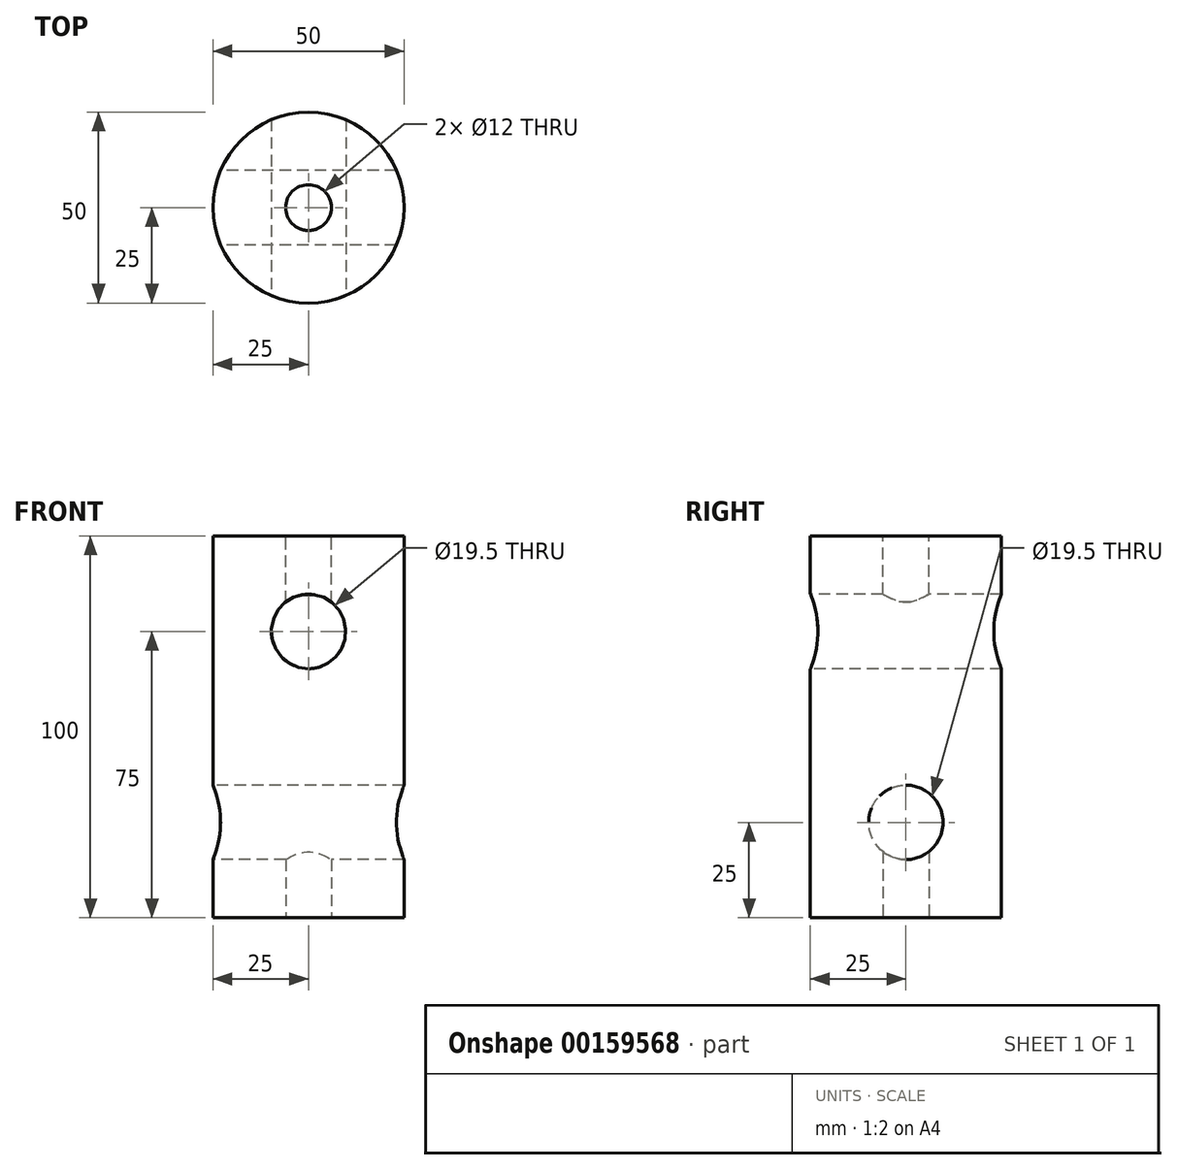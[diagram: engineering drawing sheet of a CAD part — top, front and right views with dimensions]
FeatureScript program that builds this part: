
annotation { "Feature Type Name" : "Feature", "Feature Type Description" : "" }
export const myFeature = defineFeature(function(context is Context, id is Id, definition is map)
    precondition{}
    {
        {
            var Q0;
            Q0=qCreatedBy(makeId("Top.planeOp"),FACE);
            var sketch = newSketch(context, id + "F0", { "sketchPlane" : qUnion([Q0])});
            skCircle(sketch, "E0", {"center": v(0, 0) * mm, "radius": 25 * mm});
            skSolve(sketch);
        }
        {
            var Q0;
            Q0 = qSketchRegion(id + "F0", true);
            extrude(context, id + "F1", {"entities" : qUnion([Q0]), "depth" : 100 * mm});
        }
        {
            var Q0;
            Q0=qCreatedBy(makeId("Right.planeOp"),FACE);
            var sketch = newSketch(context, id + "F2", { "sketchPlane" : qUnion([Q0])});
            skCircle(sketch, "E1", {"center": v(0, 25) * mm, "radius": 9.75 * mm});
            skSolve(sketch);
        }
        {
            var Q0;
            Q0 = qSketchRegion(id + "F2", true);
            extrude(context, id + "F3", {"entities" : qUnion([Q0]), "operationType" : NewBodyOperationType.REMOVE, "endBound" : BoundingType.THROUGH_ALL, "depth" : 25 * mm, "hasSecondDirection" : true, "secondDirectionOppositeDirection" : true, "secondDirectionDepth" : 25 * mm});
        }
        {
            var Q0;
            Q0=qCreatedBy(makeId("Front.planeOp"),FACE);
            var sketch = newSketch(context, id + "F4", { "sketchPlane" : qUnion([Q0])});
            skCircle(sketch, "E2", {"center": v(0, 75) * mm, "radius": 9.75 * mm});
            skSolve(sketch);
        }
        {
            var Q0;
            Q0 = qSketchRegion(id + "F4", true);
            extrude(context, id + "F5", {"entities" : qUnion([Q0]), "operationType" : NewBodyOperationType.REMOVE, "endBound" : BoundingType.THROUGH_ALL, "oppositeDirection" : true, "depth" : 25 * mm, "hasSecondDirection" : true, "secondDirectionOppositeDirection" : false, "secondDirectionDepth" : 25 * mm});
        }
        {
            var Q0;
            Q0=makeQuery(id+"F1.opExtrude","CAP_FACE",FACE,{"disambiguationData":[OSD([sQuery(id+"F0.wireOp",EDGE,"E0")])],"isStart":false});
            var sketch = newSketch(context, id + "F6", { "sketchPlane" : qUnion([Q0])});
            skCircle(sketch, "E3", {"center": v(0, 0) * mm, "radius": 6 * mm});
            skSolve(sketch);
        }
        {
            var Q0;
            Q0 = qSketchRegion(id + "F6", true);
            extrude(context, id + "F7", {"entities" : qUnion([Q0]), "operationType" : NewBodyOperationType.REMOVE, "oppositeDirection" : true, "depth" : 25 * mm});
        }
        {
            var Q0;
            Q0=makeQuery(id+"F1.opExtrude","CAP_FACE",FACE,{"disambiguationData":[OSD([sQuery(id+"F0.wireOp",EDGE,"E0")])],"isStart":true});
            var sketch = newSketch(context, id + "F8", { "sketchPlane" : qUnion([Q0])});
            skCircle(sketch, "E4", {"center": v(0, 0) * mm, "radius": 6 * mm});
            skSolve(sketch);
        }
        {
            var Q0;
            Q0 = qSketchRegion(id + "F8", true);
            extrude(context, id + "F9", {"entities" : qUnion([Q0]), "operationType" : NewBodyOperationType.REMOVE, "oppositeDirection" : true, "depth" : 25 * mm});
        }
    });
